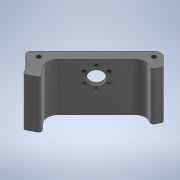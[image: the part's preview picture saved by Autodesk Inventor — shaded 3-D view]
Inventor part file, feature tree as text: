
AUTODESK INVENTOR PART (.ipt)
format: ipt  version: 2020 (Build 240168000, 168)  size: 395,264 bytes
history: native  units: mm
features: extrude x4, sketch x3, other x1, chamfer x1, fillet x1
ambient origin geometry x8: Origin, YZ Plane, XZ Plane, XY Plane, X Axis, Y Axis, Z Axis, Center Point
bodies: Body1 (feature_tree)
feature tree (10):
  other  "Твердое тело1"
  sketch  "Эскиз1"
  extrude  "Выдавливание10"  Depth=3.0mm
  sketch  "Эскиз6"
  extrude  "Выдавливание13"  Depth=6.0mm
  extrude  "Выдавливание14"  Depth=35.0mm TaperAngle=0.0deg
  chamfer  "Фаска3"  Distance=59.0mm
  extrude  "Выдавливание15"  Depth=21.2mm
  fillet  "Сопряжение1"  Radius=15.0mm
  sketch  "Эскиз7"
